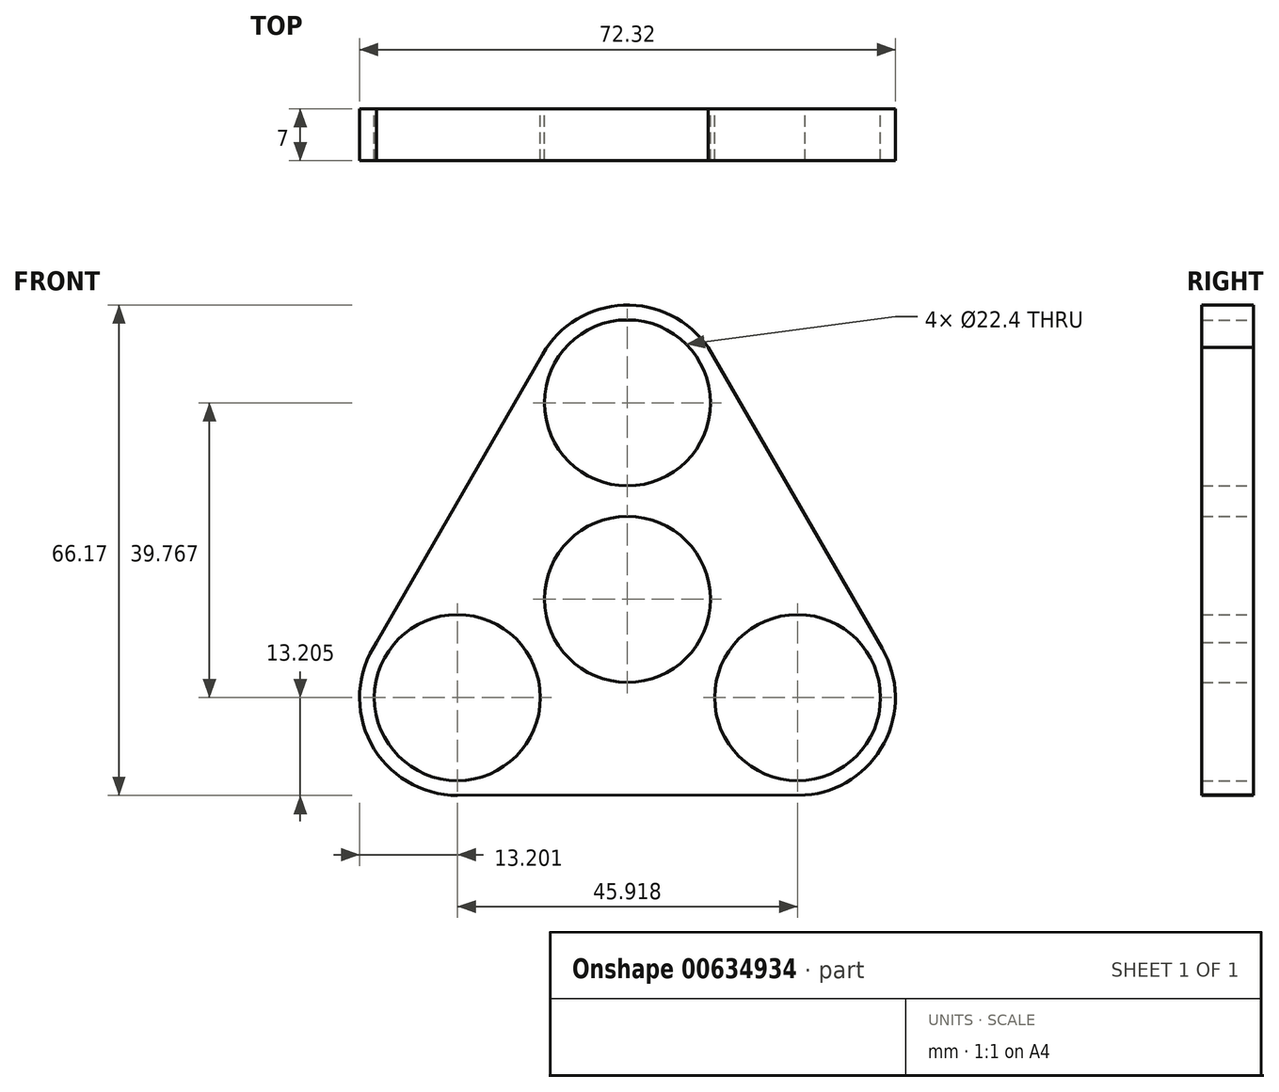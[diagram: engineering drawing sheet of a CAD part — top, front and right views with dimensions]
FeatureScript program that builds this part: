
annotation { "Feature Type Name" : "Feature", "Feature Type Description" : "" }
export const myFeature = defineFeature(function(context is Context, id is Id, definition is map)
    precondition{}
    {
        {
            var Q0;
            Q0=qCreatedBy(makeId("Front.planeOp"),FACE);
            var sketch = newSketch(context, id + "F0", { "sketchPlane" : qUnion([Q0])});
            skCircle(sketch, "E0", {"center": v(0, 0) * mm, "radius": 11.2 * mm});
            skCircle(sketch, "E1", {"center": v(0, 26.51) * mm, "radius": 11.2 * mm});
            skArc(sketch, "E2", {"start": v(11.9, 32.22) * mm, "mid": v(0.49, 39.7) * mm, "end": v(-11.45, 33.08) * mm});
            skCircle(sketch, "E3.1.0", {"center": v(-22.96, -13.26) * mm, "radius": 11.2 * mm});
            skArc(sketch, "E3.1.1", {"start": v(-33.85, -5.8) * mm, "mid": v(-34.63, -19.43) * mm, "end": v(-22.93, -26.46) * mm});
            skCircle(sketch, "E3.2.0", {"center": v(22.96, -13.26) * mm, "radius": 11.2 * mm});
            skArc(sketch, "E3.2.1", {"start": v(21.95, -26.42) * mm, "mid": v(35.8, -16.28) * mm, "end": v(27.93, -1.03) * mm});
            skLineSegment(sketch, "E4", {"start": v(-22.96, -13.26) * mm, "end": v(-9.7, -5.6) * mm, "construction": true});
            skLineSegment(sketch, "E5", {"start": v(-13.26, -7.66) * mm, "end": v(-11.53, -6.66) * mm, "construction": true});
            skLineSegment(sketch, "E6", {"start": v(16.36, -1.82) * mm, "end": v(17.36, -3.56) * mm, "construction": true});
            skLineSegment(sketch, "E7", {"start": v(29.25, 2.23) * mm, "end": v(27.93, -1.03) * mm, "construction": true});
            skLineSegment(sketch, "E8", {"start": v(10.88, 33.99) * mm, "end": v(34.39, -6.65) * mm});
            skLineSegment(sketch, "E9.1.0", {"start": v(-34.87, -7.57) * mm, "end": v(-11.44, 33.1) * mm});
            skLineSegment(sketch, "E9.2.0", {"start": v(24, -26.41) * mm, "end": v(-22.95, -26.46) * mm});
            skLineSegment(sketch, "E10.trimOffspring", {"start": v(9.7, 5.6) * mm, "end": v(11.48, 6.63) * mm, "construction": true});
            skSolve(sketch);
        }
        {
            var Q0;
            Q0=makeQuery(id+"F0.imprint","IMPRINT",FACE,{"disambiguationData":[TD([[makeQuery(id+"F0.imprint","IMPRINT",EDGE,{"derivedFrom":sQuery(id+"F0.wireOp",EDGE,"E0")}),-1.0]])]});
            extrude(context, id + "F1", {"entities" : qUnion([Q0]), "depth" : 7 * mm, "offsetDistance" : 25 * mm});
        }
    });
